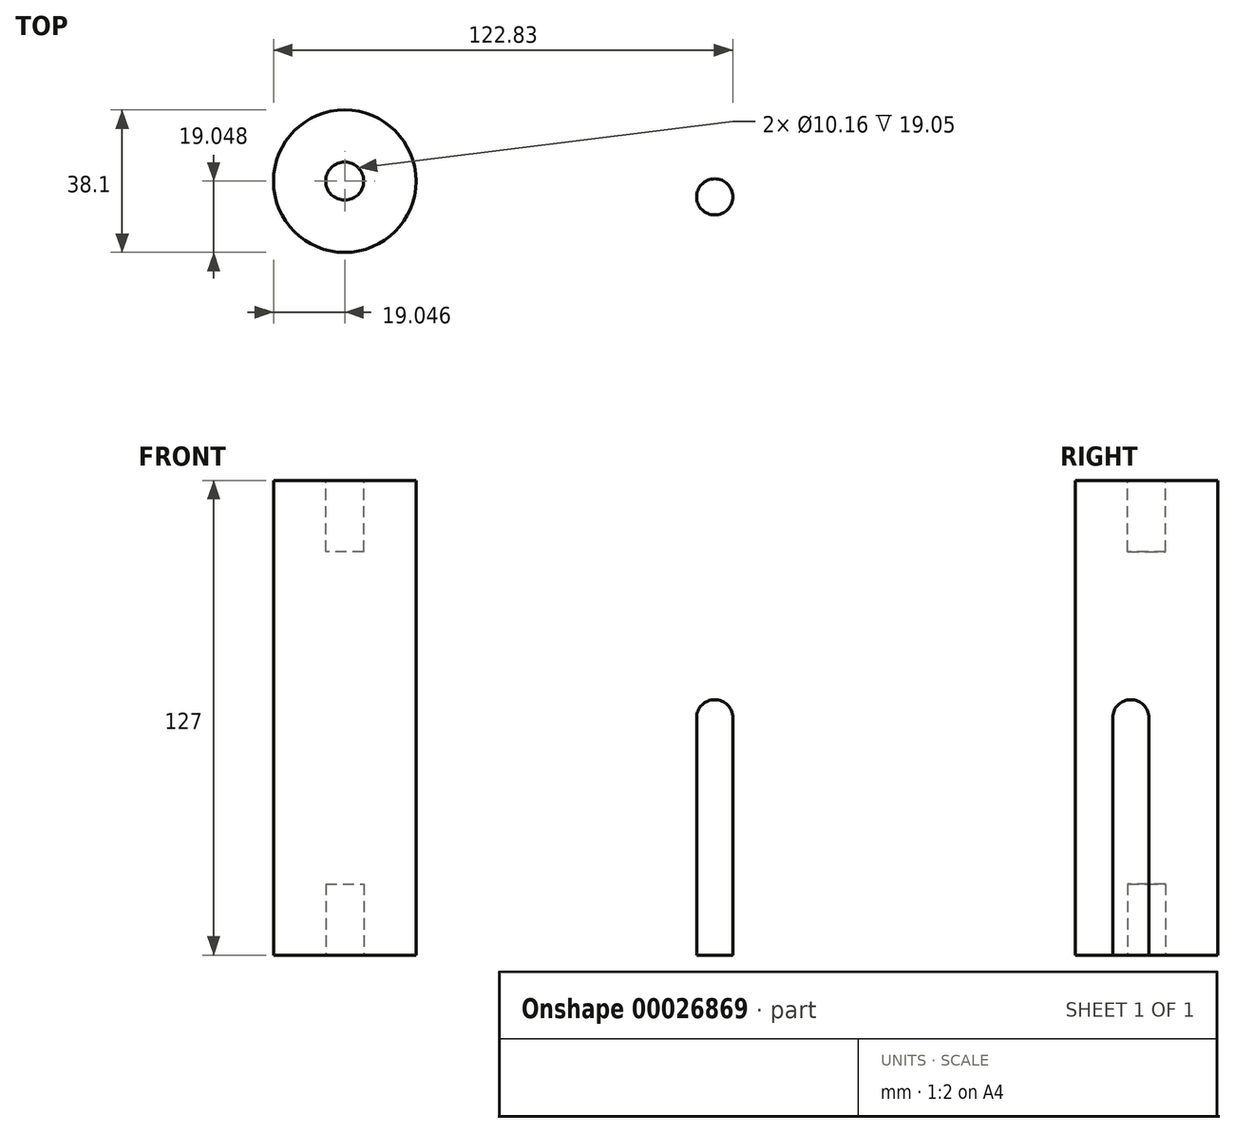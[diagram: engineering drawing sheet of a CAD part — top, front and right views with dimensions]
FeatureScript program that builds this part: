
annotation { "Feature Type Name" : "Feature", "Feature Type Description" : "" }
export const myFeature = defineFeature(function(context is Context, id is Id, definition is map)
    precondition{}
    {
        {
            var Q0;
            Q0=qCreatedBy(makeId("Top.planeOp"),FACE);
            var sketch = newSketch(context, id + "F0", { "sketchPlane" : qUnion([Q0])});
            skCircle(sketch, "E0", {"center": v(0, 0) * mm, "radius": 4.83 * mm});
            skSolve(sketch);
        }
        {
            var Q0;
            Q0=makeQuery(id+"F0.imprint","IMPRINT",FACE,{"disambiguationData":[TD([[makeQuery(id+"F0.imprint","IMPRINT",EDGE,{"derivedFrom":sQuery(id+"F0.wireOp",EDGE,"E0")}),1.0]])]});
            extrude(context, id + "F1", {"entities" : qUnion([Q0]), "depth" : 63.5 * mm});
        }
        {
            var Q0;
            Q0=makeQuery(id+"F1.opExtrude","CAP_FACE",FACE,{"disambiguationData":[OSD([sQuery(id+"F0.wireOp",EDGE,"E0")])],"isStart":false});
            var sketch = newSketch(context, id + "F2", { "sketchPlane" : qUnion([Q0])});
            skLineSegment(sketch, "E1", {"start": v(0, -4.83) * mm, "end": v(0, 4.83) * mm});
            skSolve(sketch);
        }
        {
            var Q0;
            {var subQ1=sQuery(id+"F2.wireOp",EDGE,"E1");Q0=makeQuery(id+"F2.imprint","IMPRINT",FACE,{"disambiguationData":[TD([[makeQuery(id+"F2.imprint","IMPRINT",EDGE,{"derivedFrom":subQ1}),-1.0]])]});}
            var Q1;
            Q1=sQuery(id+"F2.wireOp",EDGE,"E1");
            revolve(context, id + "F3", {"operationType" : NewBodyOperationType.ADD, "entities" : qUnion([Q0]), "axis" : qUnion([Q1]), "revolveType" : RevolveType.FULL});
        }
        {
            var Q0;
            Q0=qCreatedBy(makeId("Top.planeOp"),FACE);
            var sketch = newSketch(context, id + "F4", { "sketchPlane" : qUnion([Q0])});
            skCircle(sketch, "E2", {"center": v(-98.95, 4.2) * mm, "radius": 19.05 * mm});
            skSolve(sketch);
        }
        {
            var Q0;
            Q0=makeQuery(id+"F4.imprint","IMPRINT",FACE,{"disambiguationData":[TD([[makeQuery(id+"F4.imprint","IMPRINT",EDGE,{"derivedFrom":sQuery(id+"F4.wireOp",EDGE,"E2")}),1.0]])]});
            extrude(context, id + "F5", {"entities" : qUnion([Q0]), "depth" : 127 * mm});
        }
        {
            var Q0;
            Q0=makeQuery(id+"F5.opExtrude","CAP_FACE",FACE,{"disambiguationData":[OSD([sQuery(id+"F4.wireOp",EDGE,"E2")])],"isStart":false});
            var sketch = newSketch(context, id + "F6", { "sketchPlane" : qUnion([Q0])});
            skCircle(sketch, "E3", {"center": v(-98.95, 4.2) * mm, "radius": 5.08 * mm});
            skSolve(sketch);
        }
        {
            var Q0;
            Q0=makeQuery(id+"F5.opExtrude","CAP_FACE",FACE,{"disambiguationData":[OSD([sQuery(id+"F4.wireOp",EDGE,"E2")])],"isStart":true});
            var sketch = newSketch(context, id + "F7", { "sketchPlane" : qUnion([Q0])});
            skCircle(sketch, "E4", {"center": v(-98.95, -4.2) * mm, "radius": 5.08 * mm});
            skSolve(sketch);
        }
        {
            var Q0;
            Q0=makeQuery(id+"F7.imprint","IMPRINT",FACE,{"disambiguationData":[TD([[makeQuery(id+"F7.imprint","IMPRINT",EDGE,{"derivedFrom":sQuery(id+"F7.wireOp",EDGE,"E4")}),1.0]])]});
            extrude(context, id + "F8", {"entities" : qUnion([Q0]), "operationType" : NewBodyOperationType.REMOVE, "oppositeDirection" : true, "depth" : 19.05 * mm});
        }
        {
            var Q0;
            Q0=makeQuery(id+"F6.imprint","IMPRINT",FACE,{"disambiguationData":[TD([[makeQuery(id+"F6.imprint","IMPRINT",EDGE,{"derivedFrom":sQuery(id+"F6.wireOp",EDGE,"E3")}),1.0]])]});
            extrude(context, id + "F9", {"entities" : qUnion([Q0]), "operationType" : NewBodyOperationType.REMOVE, "oppositeDirection" : true, "depth" : 19.05 * mm});
        }
    });
